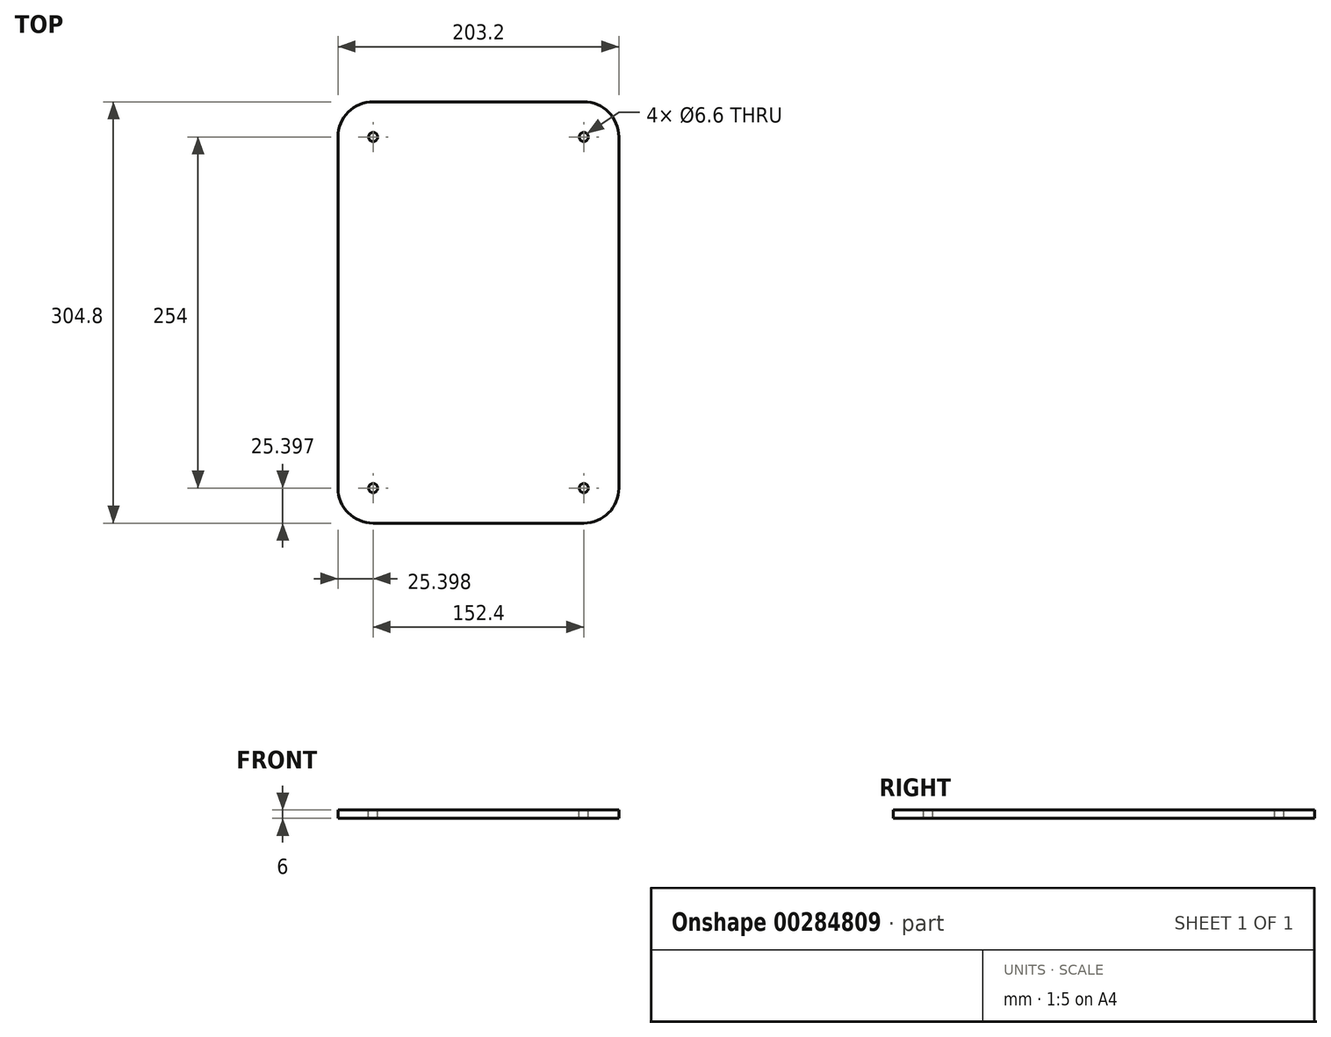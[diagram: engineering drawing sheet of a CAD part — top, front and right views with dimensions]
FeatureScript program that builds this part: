
annotation { "Feature Type Name" : "Feature", "Feature Type Description" : "" }
export const myFeature = defineFeature(function(context is Context, id is Id, definition is map)
    precondition{}
    {
        {
            var Q0;
            Q0=qCreatedBy(makeId("Top.planeOp"),FACE);
            var sketch = newSketch(context, id + "F0", { "sketchPlane" : qUnion([Q0])});
            skLineSegment(sketch, "E0.bottom", {"start": v(-95.81, -122.9) * mm, "end": v(56.59, -122.9) * mm});
            skLineSegment(sketch, "E0.top", {"start": v(-95.81, 181.9) * mm, "end": v(56.59, 181.9) * mm});
            skLineSegment(sketch, "E0.left", {"start": v(-121.21, -97.5) * mm, "end": v(-121.21, 156.5) * mm});
            skLineSegment(sketch, "E0.right", {"start": v(81.99, -97.5) * mm, "end": v(81.99, 156.5) * mm});
            skPoint(sketch, "E1.visualSharp", {"position": v(-121.21, 181.9) * mm});
            skArc(sketch, "E1.filletArc", {"start": v(-95.81, 181.9) * mm, "mid": v(-113.77, 174.47) * mm, "end": v(-121.21, 156.5) * mm});
            skPoint(sketch, "E2.visualSharp", {"position": v(81.99, 181.9) * mm});
            skArc(sketch, "E2.filletArc", {"start": v(81.99, 156.5) * mm, "mid": v(74.55, 174.47) * mm, "end": v(56.59, 181.9) * mm});
            skPoint(sketch, "E3.visualSharp", {"position": v(81.99, -122.9) * mm});
            skArc(sketch, "E3.filletArc", {"start": v(56.59, -122.9) * mm, "mid": v(74.55, -115.45) * mm, "end": v(81.99, -97.5) * mm});
            skPoint(sketch, "E4.visualSharp", {"position": v(-121.21, -122.9) * mm});
            skArc(sketch, "E4.filletArc", {"start": v(-121.21, -97.5) * mm, "mid": v(-113.77, -115.45) * mm, "end": v(-95.81, -122.9) * mm});
            skSolve(sketch);
        }
        {
            var Q0;
            Q0 = qSketchRegion(id + "F0", true);
            extrude(context, id + "F1", {"entities" : qUnion([Q0]), "depth" : 6 * mm});
        }
        {
            var Q0;
            Q0=makeQuery(id+"F1.opExtrude","CAP_FACE",FACE,{"disambiguationData":[OSD([sQuery(id+"F0.wireOp",EDGE,"E0.bottom"),sQuery(id+"F0.wireOp",EDGE,"E0.top"),sQuery(id+"F0.wireOp",EDGE,"E0.left"),sQuery(id+"F0.wireOp",EDGE,"E0.right"),sQuery(id+"F0.wireOp",EDGE,"E1.filletArc"),sQuery(id+"F0.wireOp",EDGE,"E2.filletArc"),sQuery(id+"F0.wireOp",EDGE,"E3.filletArc"),sQuery(id+"F0.wireOp",EDGE,"E4.filletArc")])],"isStart":false});
            var sketch = newSketch(context, id + "F2", { "sketchPlane" : qUnion([Q0])});
            skPoint(sketch, "E5", {"position": v(-95.81, 156.5) * mm});
            skPoint(sketch, "E6", {"position": v(56.59, 156.5) * mm});
            skPoint(sketch, "E7", {"position": v(56.59, -97.5) * mm});
            skPoint(sketch, "E8", {"position": v(-95.81, -97.5) * mm});
            skSolve(sketch);
        }
        {
            var Q0;
            Q0=sQuery(id+"F2.wireOp",VERTEX,"E5");
            var Q1;
            Q1=sQuery(id+"F2.wireOp",VERTEX,"E6");
            var Q2;
            Q2=sQuery(id+"F2.wireOp",VERTEX,"E7");
            var Q3;
            Q3=sQuery(id+"F2.wireOp",VERTEX,"E8");
            var Q4;
            Q4=makeQuery(id+"F1.opExtrude","SWEPT_BODY",BODY,{"disambiguationData":[OSD([sQuery(id+"F0.wireOp",EDGE,"E0.bottom"),sQuery(id+"F0.wireOp",EDGE,"E0.top"),sQuery(id+"F0.wireOp",EDGE,"E0.left"),sQuery(id+"F0.wireOp",EDGE,"E0.right"),sQuery(id+"F0.wireOp",EDGE,"E1.filletArc"),sQuery(id+"F0.wireOp",EDGE,"E2.filletArc"),sQuery(id+"F0.wireOp",EDGE,"E3.filletArc"),sQuery(id+"F0.wireOp",EDGE,"E4.filletArc")])]});
            hole(context, id + "F3", {"style" : HoleStyle.SIMPLE, "endStyle" : HoleEndStyle.THROUGH, "standardTappedOrClearance" : lookupTablePath({ "standard" : "ISO", "fit" : "Normal", "size" : "M6", "type" : "Clearance" }), "standardBlindInLast" : lookupTablePath({ "fit" : "Standard", "standard" : "ISO", "size" : "M6", "type" : "Clearance" }), "holeDiameter" : 6.6 * mm, "tappedDepth" : 12 * mm, "tapClearance" : 3, "locations" : qUnion([Q0, Q1, Q2, Q3]), "scope" : qUnion([Q4])});
        }
    });
